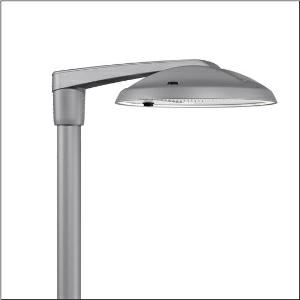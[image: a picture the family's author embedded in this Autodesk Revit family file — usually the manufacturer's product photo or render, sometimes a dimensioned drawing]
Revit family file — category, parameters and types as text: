
# Revit family: dl_r__50_iq_mini___st1_0a_5xa248d31y08me_abd5
name_source: partatom
category: Lighting Fixtures
units: mm (PartAtom-declared; Revit-internal decimal feet)

## family parameters
Cut with Voids When Loaded = No
Host = Face
Light Source = No
Part Type = Normal
Room Calculation Point = No
Round Connector Dimension = Use Diameter
Shared = No

## types (1)
- --- (1 x LED, 15720 lm, 107 W, 3000K)
    Apparent Load = 107 VA
    CIE Flux Codes = 37 72 97 100 100
    Color Rendering = 70
    Color Temperature = 3000K
    Default Elevation = 1800 mm
    Description = DL® 50 iQ mini, mast luminaire, primary light control with lens, of PMMA, primary optical cover: cover, of toughened safety glass, transparent, light distribution: ST1.0a, light emission: direct distribution, primary light characteristic: asymmetric, installation type: post-top, side-entry, LED, High Power LED, rated luminous flux: 15.720lm, luminous efficacy: 147lm/W, light colour: 730, colour temperature: 3000K, control: optimised constant luminous flux control (CLO 2.0), Desk-Remote (wireless, voltage-free reading and setting of iQ features in the workshop via application-optimized NFC function/RFID function), Light-Fading, Smart-Wire, Night-Set, Lumen-Switch, Temp-Guard, Auto-Match, Street-Remote, presetting dimming logarithmic, mains connection: 230..240V, AC, 50/60Hz, connection cable pre-assembled, cable length: 10,5m, start of lifetime: 107W, end of service life: 113W, reduction: 47W, luminaire housing, of diecast aluminium, powder-coated, Siteco® metallic grey (DB 702S), inclination adjustable: 0°, 5°, 10° (post-top) | 0°, -5°, -10°, -15° (side-entry), please order mast post-top element or mast side-entry element separately, diameter: 500mm, height: 115mm, post-top: for spigot size d x l = 76 x 100mm; with reducer (optional accessory) 60 x 100mm | side-entry: for spigot size d x l = 60 x 100mm; with reducer (optional accessory) 42 x 100mm, Smart Interface below and above, protection rating (complete): IP66, insulation class (complete): insulation class II (safety insulation), certification: CE, ENEC, VDE, impact resistance: IK08, permissible operating ambient temperature for outdoor applications: -25..+40°C, standard-compliant lighting for roads and squares, packaging unit: 1 piece

Light Distribution: ST1.0a
    Height = 115 mm
    Lamp = 1 x LED
    Lamp Light Flux = 15720 lm
    Lamp Power = 107 W
    Lamp count = 1
    Length = 500 mm
    Luminous efficacy = 147 lm/W
    Manufacturer = Siteco
    ModVariant = No
    Model = 5XA248D31Y08ME
    Number of Poles = 1
    OnlyDefault = Yes
    Power Factor = 1
    Product Name = DL® 50 iQ mini | ST1.0a
    Product group = mast luminaire | pylon top
    ProductGroupID = 6100
    Protection Class = Protection class II
    Protection Degree = IP 66
    RLX_Detail_Level = 1
    RLX_Emergency_Light_Flux = 0 lm
    RLX_Emergency_Type = 0
    RLX_Emergency_Type_DB = No
    RlxData = <blob elided: 106957 chars, md5=609d08ec>
    Socket = socket
    Standby Power = 0 W
    System Light Flux = 15720 lm
    System Power = 107 W
    Type Comments = factory setting: luminous flux: 100 % | dim-lin: 254 | 565 mA
    Type Image = l_1251786.jpg
    URL = http://relux.com
    VarID = @adj_024183
    Voltage = 0 V
    Weight = 0.00 kg
    Width = 0 mm  [stored 0 ft]

note: [stored X ft] marks values corroborated as IEEE doubles in the binary element streams (Revit-internal decimal feet)

## geometry (parser evidence)
native form markers: Blend x4, Sweep x10
no freeform markers — native parametric forms only
